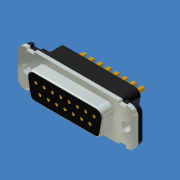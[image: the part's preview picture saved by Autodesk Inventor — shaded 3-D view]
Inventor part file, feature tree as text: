
AUTODESK INVENTOR PART (.ipt)
format: ipt  version: unknown  size: 509,952 bytes
history: native  units: mm (DEFAULTED — no unit token found)
features: extrude x14, pattern_linear x7, sketch x4, fillet x4, chamfer x3
ambient origin geometry x8: Origin, YZ Plane, XZ Plane, XY Plane, X Axis, Y Axis, Z Axis, Center Point
feature tree (32):
  sketch  "Sketch1"  dims[d0=1.745329mm d6=0.381mm d7=2.418418mm d8=0.855895mm d9=2.418418mm]
  extrude  "Extrusion1"  Depth=0.381mm
  extrude  "Extrusion2"  Depth=2.54mm
  fillet  "Fillet4"  Radius=1.397mm
  extrude  "Pin1"  Depth=5.08mm TaperAngle=0.0deg
  extrude  "Pin2"  Depth=5.08mm TaperAngle=0.0deg
  extrude  "Pin50"  Depth=80.0mm
  fillet  "Fillet1"  Radius=2.794mm
  fillet  "Fillet2"  Radius=70.0mm
  fillet  "Fillet50"  Radius=2.794mm
  extrude  "Extrusion5"  Depth=1.909443mm
  extrude  "Extrusion6"  Depth=0.254mm
  sketch  "Sketch4"  dims[d24=5.08mm d25=0.0mm d26=5.08mm d27=0.0mm d28=80.0mm d30=2.794mm d31=70.0mm d33=2.794mm d34=1.909443mm d35=0.254mm d36=1.6002mm d37=0.0mm d38=5.08mm d39=0.0mm d40=5.08mm d41=0.0mm d42=5.08mm d43=0.0mm d44=0.4953mm d45=0.4953mm d46=1.016mm d47=0.3048mm d48=0.3048mm d49=0.3048mm d50=0.3048mm d52=2.8448mm d53=5.08mm d54=0.0mm d55=0.4953mm d56=5.08mm d57=0.0mm d58=0.2032mm d59=0.2032mm d60=80.0mm d62=2.794mm d63=0.381mm d64=20.0mm d66=2.794mm d67=5.1054mm d68=0.0mm d69=5.6388mm d70=0.0mm d71=5.6388mm d72=0.0mm d73=5.6388mm d74=0.0mm d75=80.0mm d77=2.794mm d78=70.0mm d80=2.794mm d81=80.0mm d83=2.794mm d86=1.909443mm d87=10.4394mm d88=27.2034mm d89=45.0deg d90=45.0deg d91=45.0deg]
  extrude  "Extrusion7"  Depth=1.6002mm TaperAngle=0.0deg
  extrude  "Extrusion8"  Depth=5.08mm TaperAngle=0.0deg
  extrude  "ExtrudeSgr50"  Depth=5.08mm TaperAngle=0.0deg
  chamfer  "Chamfer1"  Distance=5.08mm
  chamfer  "Chamfer2"  Distance=0.4953mm
  chamfer  "Chamfer50"  Distance=0.4953mm
  pattern_linear  "Pattern1"  Spacing1=1.016mm  [1 undecoded]
  pattern_linear  "Pattern2"  Spacing1=0.3048mm  [1 undecoded]
  pattern_linear  "Pattern50"  Spacing1=0.3048mm  [1 undecoded]
  pattern_linear  "Pattern15"  Spacing1=0.3048mm  [1 undecoded]
  extrude  "Female"  Depth=0.3048mm
  extrude  "Socket1"  Depth=2.8448mm
  extrude  "Socket2"  Depth=5.08mm
  extrude  "Socket50"  TaperAngle=0.0deg  [1 undecoded]
  pattern_linear  "Pattern5"  Spacing1=0.4953mm  [1 undecoded]
  pattern_linear  "Pattern6"  Spacing1=5.08mm  [1 undecoded]
  pattern_linear  "Pattern7"  Spacing1=0.0mm  [1 undecoded]
  sketch  "Sketch2"  dims[d11=1.314425mm d15=2.54mm d19=1.397mm]
  sketch  "Sketch3"  dims[d20=1.27mm d21=0.0mm d22=5.08mm d23=0.0mm]
note: 8 required parameter values undecoded (feature->parameter linkage not recoverable at this tier; creation-order binding heuristic only, values carry confidence <= 0.55)
